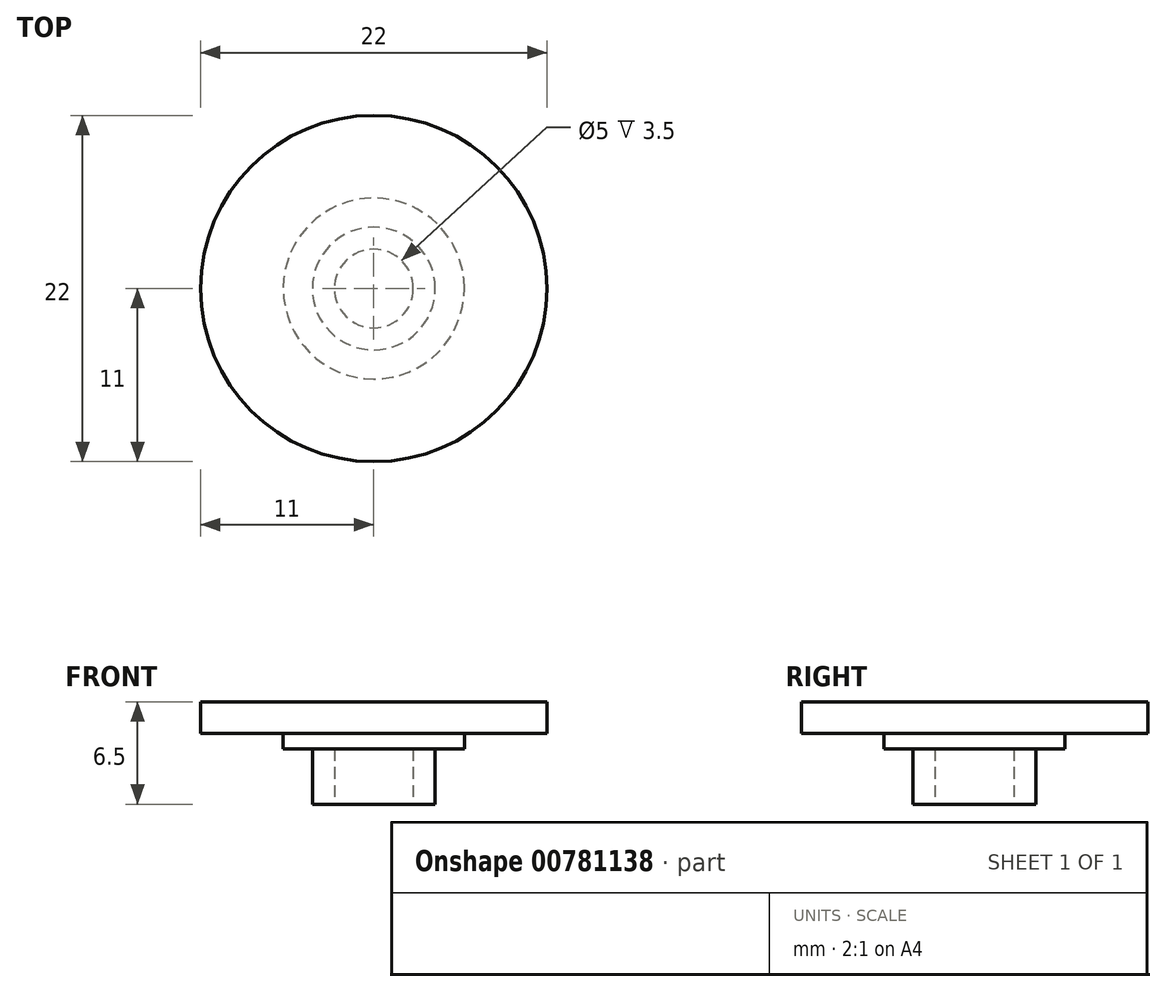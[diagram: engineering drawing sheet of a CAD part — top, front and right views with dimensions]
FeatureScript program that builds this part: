
annotation { "Feature Type Name" : "Feature", "Feature Type Description" : "" }
export const myFeature = defineFeature(function(context is Context, id is Id, definition is map)
    precondition{}
    {
        {
            var Q0;
            Q0=qCreatedBy(makeId("Top.planeOp"),FACE);
            var sketch = newSketch(context, id + "F0", { "sketchPlane" : qUnion([Q0])});
            skCircle(sketch, "E0", {"center": v(0, 0) * mm, "radius": 11 * mm});
            skSolve(sketch);
        }
        {
            var Q0;
            Q0=makeQuery(id+"F0.imprint","IMPRINT",FACE,{"disambiguationData":[TD([[makeQuery(id+"F0.imprint","IMPRINT",EDGE,{"derivedFrom":sQuery(id+"F0.wireOp",EDGE,"E0")}),1.0]])]});
            extrude(context, id + "F1", {"entities" : qUnion([Q0]), "depth" : 6.5 * mm, "offsetDistance" : 25 * mm, "hasSecondDirection" : true, "secondDirectionOppositeDirection" : false, "secondDirectionDepth" : 4.5 * mm});
        }
        {
            var Q0;
            Q0=qCreatedBy(makeId("Top.planeOp"),FACE);
            var sketch = newSketch(context, id + "F2", { "sketchPlane" : qUnion([Q0])});
            skCircle(sketch, "E1", {"center": v(0, 0) * mm, "radius": 3.9 * mm});
            skCircle(sketch, "E2", {"center": v(0, 0) * mm, "radius": 2.5 * mm});
            skSolve(sketch);
        }
        {
            var Q0;
            Q0=makeQuery(id+"F2.imprint","IMPRINT",FACE,{"disambiguationData":[TD([[makeQuery(id+"F2.imprint","IMPRINT",EDGE,{"derivedFrom":sQuery(id+"F2.wireOp",EDGE,"E1")}),1.0]])]});
            extrude(context, id + "F3", {"entities" : qUnion([Q0]), "operationType" : NewBodyOperationType.ADD, "depth" : 3.5 * mm, "offsetDistance" : 25 * mm});
        }
        {
            var Q0;
            Q0=qCreatedBy(makeId("Top.planeOp"),FACE);
            var sketch = newSketch(context, id + "F4", { "sketchPlane" : qUnion([Q0])});
            skCircle(sketch, "E3", {"center": v(0, 0) * mm, "radius": 5.75 * mm});
            skSolve(sketch);
        }
        {
            var Q0;
            Q0=makeQuery(id+"F4.imprint","IMPRINT",FACE,{"disambiguationData":[TD([[makeQuery(id+"F4.imprint","IMPRINT",EDGE,{"derivedFrom":sQuery(id+"F4.wireOp",EDGE,"E3")}),1.0]])]});
            extrude(context, id + "F5", {"entities" : qUnion([Q0]), "operationType" : NewBodyOperationType.ADD, "depth" : 4.5 * mm, "offsetDistance" : 25 * mm, "hasSecondDirection" : true, "secondDirectionOppositeDirection" : false, "secondDirectionDepth" : 3.5 * mm});
        }
    });
